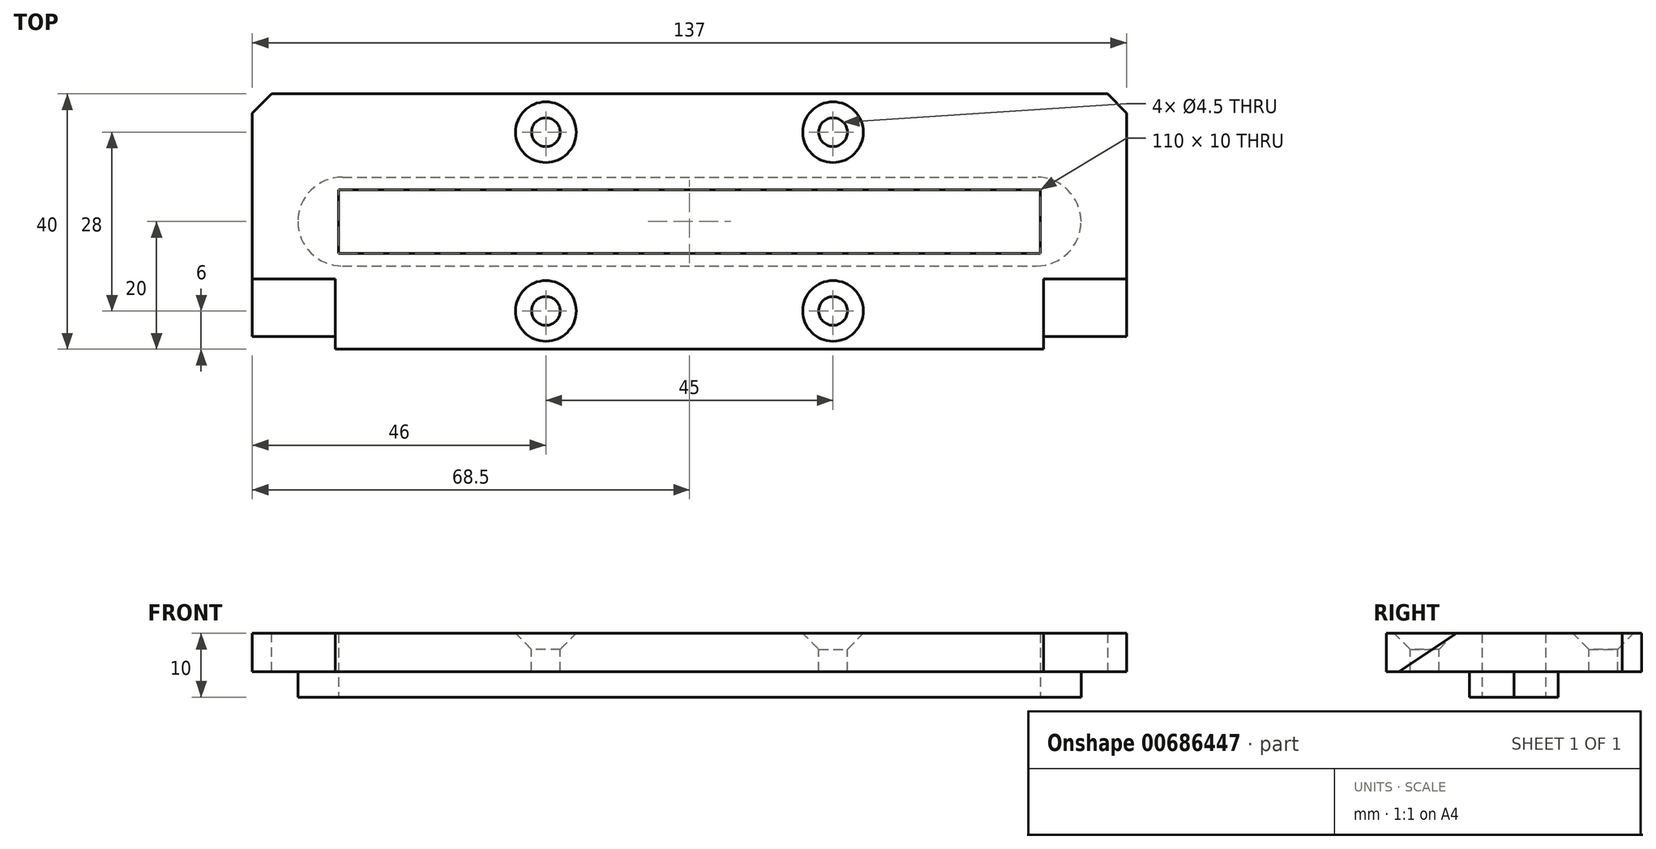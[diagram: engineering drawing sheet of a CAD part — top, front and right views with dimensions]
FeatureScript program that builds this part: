
annotation { "Feature Type Name" : "Feature", "Feature Type Description" : "" }
export const myFeature = defineFeature(function(context is Context, id is Id, definition is map)
    precondition{}
    {
        {
            var Q0;
            Q0=qCreatedBy(makeId("Top.planeOp"),FACE);
            var sketch = newSketch(context, id + "F0", { "sketchPlane" : qUnion([Q0])});
            skLineSegment(sketch, "E0.bottom", {"start": v(-68.5, 20) * mm, "end": v(0, 20) * mm});
            skLineSegment(sketch, "E0.top", {"start": v(-68.5, -20) * mm, "end": v(0, -20) * mm});
            skLineSegment(sketch, "E0.left", {"start": v(-68.5, 20) * mm, "end": v(-68.5, -20) * mm});
            skLineSegment(sketch, "E1.bottom", {"start": v(-55, 5) * mm, "end": v(0, 5) * mm});
            skLineSegment(sketch, "E1.top", {"start": v(-55, -5) * mm, "end": v(0, -5) * mm});
            skLineSegment(sketch, "E1.left", {"start": v(-55, 5) * mm, "end": v(-55, -5) * mm});
            skLineSegment(sketch, "E2", {"start": v(0, 20) * mm, "end": v(0, -20) * mm});
            skPoint(sketch, "E0.right.end.orphan", {"position": v(68.5, -20) * mm});
            skPoint(sketch, "E3.orphan", {"position": v(68.5, 20) * mm});
            skSolve(sketch);
        }
        {
            var Q0;
            Q0=makeQuery(id+"F0.imprint","IMPRINT",FACE,{"disambiguationData":[TD([[makeQuery(id+"F0.imprint","IMPRINT",EDGE,{"derivedFrom":sQuery(id+"F0.wireOp",EDGE,"E0.bottom")}),-1.0]])]});
            extrude(context, id + "F1", {"entities" : qUnion([Q0]), "depth" : 6 * mm, "offsetDistance" : 25 * mm});
        }
        {
            var Q0;
            Q0=makeQuery(id+"F1.opExtrude","SWEPT_FACE",FACE,{"disambiguationData":[OSD([sQuery(id+"F0.wireOp",EDGE,"E0.left")])]});
            var sketch = newSketch(context, id + "F2", { "sketchPlane" : qUnion([Q0])});
            skLineSegment(sketch, "E4", {"start": v(20, 6) * mm, "end": v(9, 6) * mm});
            skLineSegment(sketch, "E5", {"start": v(9, 6) * mm, "end": v(18, 0) * mm});
            skLineSegment(sketch, "E6", {"start": v(18, 0) * mm, "end": v(20, 0) * mm});
            skLineSegment(sketch, "E7", {"start": v(20, 0) * mm, "end": v(20, 6) * mm});
            skSolve(sketch);
        }
        {
            var Q0;
            Q0=makeQuery(id+"F2.imprint","IMPRINT",FACE,{"disambiguationData":[TD([[makeQuery(id+"F2.imprint","IMPRINT",EDGE,{"derivedFrom":sQuery(id+"F2.wireOp",EDGE,"E4")}),-1.0]])]});
            extrude(context, id + "F3", {"entities" : qUnion([Q0]), "operationType" : NewBodyOperationType.REMOVE, "oppositeDirection" : true, "depth" : 13 * mm, "offsetDistance" : 25 * mm});
        }
        {
            var Q0;
            {var subQ0=makeQuery(id+"F1.opExtrude","CAP_FACE",FACE,{"disambiguationData":[OSD([sQuery(id+"F0.wireOp",EDGE,"E0.bottom"),sQuery(id+"F0.wireOp",EDGE,"E0.top"),sQuery(id+"F0.wireOp",EDGE,"E0.left"),sQuery(id+"F0.wireOp",EDGE,"E1.bottom"),sQuery(id+"F0.wireOp",EDGE,"E1.top"),sQuery(id+"F0.wireOp",EDGE,"E1.left"),sQuery(id+"F0.wireOp",EDGE,"E2")])],"isStart":false});Q0=makeQuery(id+"F6.boolean.opBoolean","MERGE",FACE,{"derivedFrom":[subQ0,makeQuery(id+"F6.opPattern","COPY",FACE,{"derivedFrom":subQ0,"instanceName":"1"})]});}
            var sketch = newSketch(context, id + "F4", { "sketchPlane" : qUnion([Q0])});
            skPoint(sketch, "E8", {"position": v(-22.5, 14) * mm});
            skPoint(sketch, "E9", {"position": v(-22.5, -14) * mm});
            skSolve(sketch);
        }
        {
            var Q0;
            Q0=sQuery(id+"F4.wireOp",VERTEX,"E8");
            var Q1;
            Q1=sQuery(id+"F4.wireOp",VERTEX,"E9");
            var Q2;
            Q2=makeQuery(id+"F1.opExtrude","SWEPT_BODY",BODY,{"disambiguationData":[OSD([sQuery(id+"F0.wireOp",EDGE,"E0.bottom"),sQuery(id+"F0.wireOp",EDGE,"E0.top"),sQuery(id+"F0.wireOp",EDGE,"E0.left"),sQuery(id+"F0.wireOp",EDGE,"E1.bottom"),sQuery(id+"F0.wireOp",EDGE,"E1.top"),sQuery(id+"F0.wireOp",EDGE,"E1.left"),sQuery(id+"F0.wireOp",EDGE,"E2")])]});
            hole(context, id + "F5", {"style" : HoleStyle.C_SINK, "endStyle" : HoleEndStyle.THROUGH, "holeDiameter" : 4.5 * mm, "cSinkDiameter" : 9.5 * mm, "cSinkAngle" : 90 * degree, "majorDiameter" : 5 * mm, "isTappedThrough" : true, "tappedDepth" : 12 * mm, "tapClearance" : 3, "startFromSketch" : true, "locations" : qUnion([Q0, Q1]), "scope" : qUnion([Q2])});
        }
        {
            var Q0;
            Q0=makeQuery(id+"F1.opExtrude","SWEPT_BODY",BODY,{"disambiguationData":[OSD([sQuery(id+"F0.wireOp",EDGE,"E0.bottom"),sQuery(id+"F0.wireOp",EDGE,"E0.top"),sQuery(id+"F0.wireOp",EDGE,"E0.left"),sQuery(id+"F0.wireOp",EDGE,"E1.bottom"),sQuery(id+"F0.wireOp",EDGE,"E1.top"),sQuery(id+"F0.wireOp",EDGE,"E1.left"),sQuery(id+"F0.wireOp",EDGE,"E2")])]});
            var Q1;
            Q1=qCreatedBy(makeId("Right.planeOp"),FACE);
            mirror(context, id + "F6", {"operationType" : NewBodyOperationType.ADD, "entities" : qUnion([Q0]), "mirrorPlane" : qUnion([Q1])});
        }
        {
            var Q0;
            {var subQ0=makeQuery(id+"F1.opExtrude","CAP_FACE",FACE,{"disambiguationData":[OSD([sQuery(id+"F0.wireOp",EDGE,"E0.bottom"),sQuery(id+"F0.wireOp",EDGE,"E0.top"),sQuery(id+"F0.wireOp",EDGE,"E0.left"),sQuery(id+"F0.wireOp",EDGE,"E1.bottom"),sQuery(id+"F0.wireOp",EDGE,"E1.top"),sQuery(id+"F0.wireOp",EDGE,"E1.left"),sQuery(id+"F0.wireOp",EDGE,"E2")])],"isStart":true});Q0=makeQuery(id+"F6.boolean.opBoolean","MERGE",FACE,{"derivedFrom":[subQ0,makeQuery(id+"F6.opPattern","COPY",FACE,{"derivedFrom":subQ0,"instanceName":"1"})]});}
            var sketch = newSketch(context, id + "F7", { "sketchPlane" : qUnion([Q0])});
            skLineSegment(sketch, "E10.bottom", {"start": v(-54.37, 6.96) * mm, "end": v(54.38, 6.96) * mm});
            skLineSegment(sketch, "E10.top", {"start": v(-54.38, -6.95) * mm, "end": v(54.38, -6.95) * mm});
            skLineSegment(sketch, "E10.left", {"start": v(-61.38, 0.04) * mm, "end": v(-61.38, -0.05) * mm});
            skLineSegment(sketch, "E10.right", {"start": v(61.38, 0.05) * mm, "end": v(61.38, -0.04) * mm});
            skLineSegment(sketch, "E11.bottom", {"start": v(-55, -5) * mm, "end": v(55, -5) * mm});
            skLineSegment(sketch, "E11.top", {"start": v(-55, 5) * mm, "end": v(55, 5) * mm});
            skLineSegment(sketch, "E11.left", {"start": v(-55, -5) * mm, "end": v(-55, 5) * mm});
            skLineSegment(sketch, "E11.right", {"start": v(55, -5) * mm, "end": v(55, 5) * mm});
            skPoint(sketch, "E12.visualSharp", {"position": v(61.38, 6.96) * mm});
            skArc(sketch, "E12.filletArc", {"start": v(61.38, -0.04) * mm, "mid": v(59.32, 4.9) * mm, "end": v(54.38, 6.96) * mm});
            skPoint(sketch, "E13.visualSharp", {"position": v(61.38, -6.95) * mm});
            skArc(sketch, "E13.filletArc", {"start": v(54.38, -6.95) * mm, "mid": v(59.32, -4.9) * mm, "end": v(61.38, 0.05) * mm});
            skPoint(sketch, "E14.visualSharp", {"position": v(-61.38, 6.96) * mm});
            skArc(sketch, "E14.filletArc", {"start": v(-54.38, 6.95) * mm, "mid": v(-59.32, 4.9) * mm, "end": v(-61.38, -0.05) * mm});
            skPoint(sketch, "E15.visualSharp", {"position": v(-61.38, -6.96) * mm});
            skArc(sketch, "E15.filletArc", {"start": v(-61.38, 0.04) * mm, "mid": v(-59.32, -4.9) * mm, "end": v(-54.38, -6.96) * mm});
            skSolve(sketch);
        }
        {
            var Q0;
            {var subQ4=sQuery(id+"F7.wireOp",EDGE,"E10.bottom");Q0=makeQuery(id+"F7.imprint","IMPRINT",FACE,{"disambiguationData":[TD([[makeQuery(id+"F7.imprint","IMPRINT",EDGE,{"derivedFrom":subQ4}),-1.0]])]});}
            extrude(context, id + "F8", {"entities" : qUnion([Q0]), "operationType" : NewBodyOperationType.ADD, "depth" : 4 * mm, "offsetDistance" : 25 * mm});
        }
        {
            var Q0;
            Q0=makeQuery(id+"F1.opExtrude","SWEPT_EDGE",EDGE,{"disambiguationData":[OSD([sQuery(id+"F0.wireOp",EDGE,"E0.bottom"),sQuery(id+"F0.wireOp",EDGE,"E0.left")])]});
            var Q1;
            Q1=makeQuery(id+"F6.opPattern","COPY",EDGE,{"derivedFrom":makeQuery(id+"F1.opExtrude","SWEPT_EDGE",EDGE,{"disambiguationData":[OSD([sQuery(id+"F0.wireOp",EDGE,"E0.bottom"),sQuery(id+"F0.wireOp",EDGE,"E0.left")])]}),"instanceName":"1"});
            chamfer(context, id + "F9", {"entities" : qUnion([Q0, Q1]), "width" : 3 * mm, "tangentPropagation" : true});
        }
    });
